# Revit family: FORM-20-REC-CM_with_ESC_Lens_Lighting_Non-Hosted_R20
name_source: partatom
category: Lighting Fixtures
units: mm (PartAtom-declared; Revit-internal decimal feet)

## family parameters
Always vertical = Yes
Cut with Voids When Loaded = No
Light Source = Yes
OmniClass Number = 23.80.70.00
OmniClass Title = Lighting
Part Type = Normal
Room Calculation Point = No
Round Connector Dimension = Use Diameter
Shared = No
Work Plane-Based = No

## types (6) — shared parameters
Applicable Standards = BS EN 55015, BS EN 61547, BS EN 61000-3-2, BS EN 61000-3-3, ETSI EN 301 489-1, ETSI EN 301 489-17, BS EN 1838, BS EN ISO 7010, BS EN 62471, BS EN 62031, BS EN 60598-2-22
Charging Method = Intelligent Current Limited Constant Voltage
Color Filter = 16777215
Construction = PCM Box with PC/Aluminium Extrusion Blade
Diffuser = Polycarbonate
Dimensions (L x W x H) = 220 x 18 x 110
Dimming Lamp Color Temperature Shift = <None>
Earth Leakage = 0.35
Emit Shape Visible in Rendering = No
IK Rating = IK03
IP Rating = IP20
Inrush Current (Max) = 10A<144µs
Manufacturer = Clevertronics
Mounting = Recessed Ceiling Mount, Double Sided
Operating Mode = Maintained
Operating Temperature = 0 ºC - 40ºC
Operating Voltage = 220-240V~ 50Hz
Photometric Web File = generic
Power Factor = 0.28 (Standby, Maintained), 0.42 (Max)
Tilt Angle = 90.00°
Weight = 0.75kg
zero-valued in all types: Default Elevation

## per-type parameters (varying)
| type | Battery | Battery Type | Description | MIC Number | Power Consumption | Power Consumption (Standby - Lamp Off) | Replacement Battery | Replacement Emergency Driver | Replacement Item | Supply Current | Testing System | Type Comments |
| FORM-20-REC-CM-LP-HVG-ESC | 3.2V 3200mAh | Lithium Iron Phosphate | Form 20m Exit, Recessed Ceiling Mount, CLP, Zoneworks XT Hive, Picto All, Double Sided, Escape Route Illumination, Brushed Aluminium Frame | UKA02810160001 | 3.6W | 1.5W | 1550050 | UKM02870300001 - CLEDDRV2CH-RR-2C170-6C30-15-CKIT-HVGEXTA | 8003345 | 19.91 (Standby, Maintained), 35.60 (Max) - (mA) | Zoneworks XT HIVE (RF | Form 20M Exit, Rec CM, CLP, ZW HT Hive, ESC, Alm |
| FORM-20-REC-CM-LP-ESC | 3.2V 3200mAh | Lithium Iron Phosphate | Form 20m Exit, Recessed Ceiling Mount, CLP, Clevertest Plus, Picto All, Double Sided, Escape Route Illumination, Brushed Aluminium Frame | UKA02310170001 | 3.3W | 1.2W | 1550050 | UKM02370210001 - CLEDDRV2CH-RR-2C170-6C30-15-CKIT |  | 18.61 (Standby, Maintained), 34.30 (Max) - (mA) | Clevertest Plus Enabled (Not Activated By Default) | Form 20M Exit, Rec CM, CLP, CTP, ESC, Alm |
| FORM-20-REC-CM-LP-DALI-ESC | 3.2V 3200mAh | Lithium Iron Phosphate | Form 20m Exit, Recessed Ceiling Mount, CLP, DALI Emergency, Picto All, Double Sided, Escape Route Illumination, Brushed Aluminium Frame | UKA02210160002 | 3.6W | 1.5W | 1550050 | UKM02270080002 - CLEDDRV2CH-RR-2C170-6C30-15-CKIT-DALI | 8003068 | 19.91 (Standby, Maintained), 35.60 (Max) - (mA) | DALI Registered | Form 20M Exit, Rec CM, CLP, Dali Reg, ESC, Alm |
| FORM-20-REC-CM-L10-HVG-ESC | 3.3V 2500mAh | Lithium Nanophosphate | Form 20m Exit, Recessed Ceiling Mount, L10 Nanophosphate, Zoneworks XT Hive, Picto All, Double Sided, Escape Route Illumination, Brushed Aluminium Frame | UKA01810320001 | 3.6W | 1.5W | 1530050 | UKM01870370001 - LLEDDRV2CH-RR-2C170-6C30-15-CKIT-HVGEXTA | 8003345 | 19.91 (Standby, Maintained), 35.60 (Max) - (mA) | Zoneworks XT HIVE (RF) | Form 20M Exit, Rec CM, L10, ZW HT Hive, ESC, Alm |
| FORM-20-REC-CM-L10-ESC | 3.3V 2500mAh | Lithium Nanophosphate | Form 20m Exit, Recessed Ceiling Mount, L10 Nanophosphate, Clevertest Plus, Picto All, Double Sided, Escape Route Illumination, Brushed Aluminium Frame | UKA01310190001 | 3.3W | 1.2W | 1530050 | UKM01370300001 - LLEDDRV2CH-RR-2C170-6C30-15-CKIT |  | 18.61 (Standby, Maintained), 34.30 (Max) - (mA) | Clevertest Plus Enabled (Not Activated By Default) | Form 20M Exit, Rec CM, L10, CTP, ESC, Alm |
| FORM-20-REC-CM-L10-DALI-ESC | 3.3V 2500mAh | Lithium Nanophosphate | Form 20m Exit, Recessed Ceiling Mount, L10 Nanophosphate, DALI Emergency, Picto All, Double Sided, Escape Route Illumination, Brushed Aluminium Frame | UKA01210160002 | 3.6W | 1.5W | 1530050 | UKM01270080002 - LLEDDRV2CH-RR-2C170-6C30-15-CKIT-DALI | 8003068 | 19.91 (Standby, Maintained), 35.60 (Max) - (mA) | DALI Registered | Form 20M Exit, Rec CM, L10, Dali Reg, ESC, Alm |

note: column(s) folded — value = type name in every type: Model

## geometry (parser evidence)
native form markers: Extrusion x8, Sweep x3
no freeform markers — native parametric forms only
